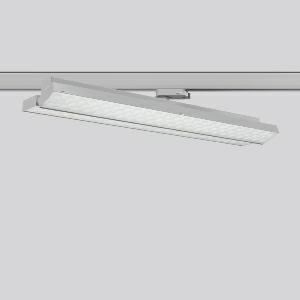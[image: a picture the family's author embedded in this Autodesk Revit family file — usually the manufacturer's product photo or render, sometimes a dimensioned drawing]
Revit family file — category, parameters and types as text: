
# Revit family: tx-move_742162_004_2_76_fdef
name_source: partatom
category: Lighting Fixtures
units: mm (PartAtom-declared; Revit-internal decimal feet)

## family parameters
Cut with Voids When Loaded = No
Host = Face
Light Source = No
Part Type = Normal
Room Calculation Point = No
Round Connector Dimension = Use Diameter
Shared = No

## types (1)
- MultiLumen 1 (1 x LED Modul 927, 2100 lm, 2700)
    Apparent Load = 38 VA
    CIE Flux Codes = 77 96 99 100 100
    Color Rendering = 92
    Color Temperature = 2700
    Default Elevation = 1800 mm
    Description = Series: TX-MOVE
Multifunctional surface-mounted spotlight for area lighting. Very flat design. Housing: sheet steel, powder-coated. Rotation range: 356°. Swivel range: 90°. Consistent alignment possible with visible tilt scale. High-efficiency LED units with optimum light control thanks to clear plastic (PC) lens optics. Spezielle Mikrostrukturen reduzieren Gelbsaum. Symmetrical light distribution. Best colour rendering with CRI >90 for fresh products and coloured textiles. With adapter for RZB 3-circuit DALI tracks. Suitable for Track on ceiling. MultiLumen: Luminous flux adjustable in 3 steps. Factory setting is the highest luminous flux. Environmentally friendly and resource-saving due to replaceable and recyclable components. 
Colour: silver, matt (approx. RAL 9006)
Length: 570 mm
Width: 119 mm
Height: 88 mm
Lamp: LED
Socket: without socket
Colour temperature: 2700K
Colour rendering index (CRI): 90
System power: 38 W
Rated luminous flux: 4200 lm
Luminous efficiency: 111 lm/W
System power 2: 51 W
Rated luminous flux 2: 5500 lm
Luminous efficiency 2: 108 lm/W
System power 3: 62 W
Rated luminous flux 3: 6550 lm
Luminous efficiency 3: 106 lm/W
Control gear: Dimmable EVG, DALI
Protection class: I
Type of protection: IP 20
    Height = 75 mm
    Lamp = 1 x LED Modul 927
    Lamp Light Flux = 2100 lm
    Lamp count = 1
    Length = 569 mm
    Lifetime = 50000 h
    Luminous efficacy = 111 lm/W
    Manufacturer = RZB
    ModVariant = No
    Model = 742162.004.2.76
    Mounting Place = Ceiling
    Mounting Type = Surface mounted
    Number of Poles = 1
    OnlyDefault = Yes
    Power Factor = 1
    Product Name = TX-MOVE
    Product group = Track mounted projectors
    ProductGroupID = 301
    Protection Class = Protection class I
    Protection Degree = IP 20
    RLX_Detail_Level = 1
    RLX_Emergency_Light_Flux = 0 lm
    RLX_Emergency_Type = 0
    RLX_Emergency_Type_DB = No
    RlxData = <blob elided: 33285 chars, md5=b9b4e33d>
    Socket = socket
    Standby Power = 0 W
    System Light Flux = 4200 lm
    System Power = 38 W
    Type Comments = MultiLumen 1
    Type Image = 742162.004.jpg
    URL = http://relux.com
    VarID = multilumen_1
    Voltage = 0 V
    Weight = 0.00 kg
    Width = 119 mm

## geometry (parser evidence)
native form markers: Blend x4, Sweep x14
no freeform markers — native parametric forms only
